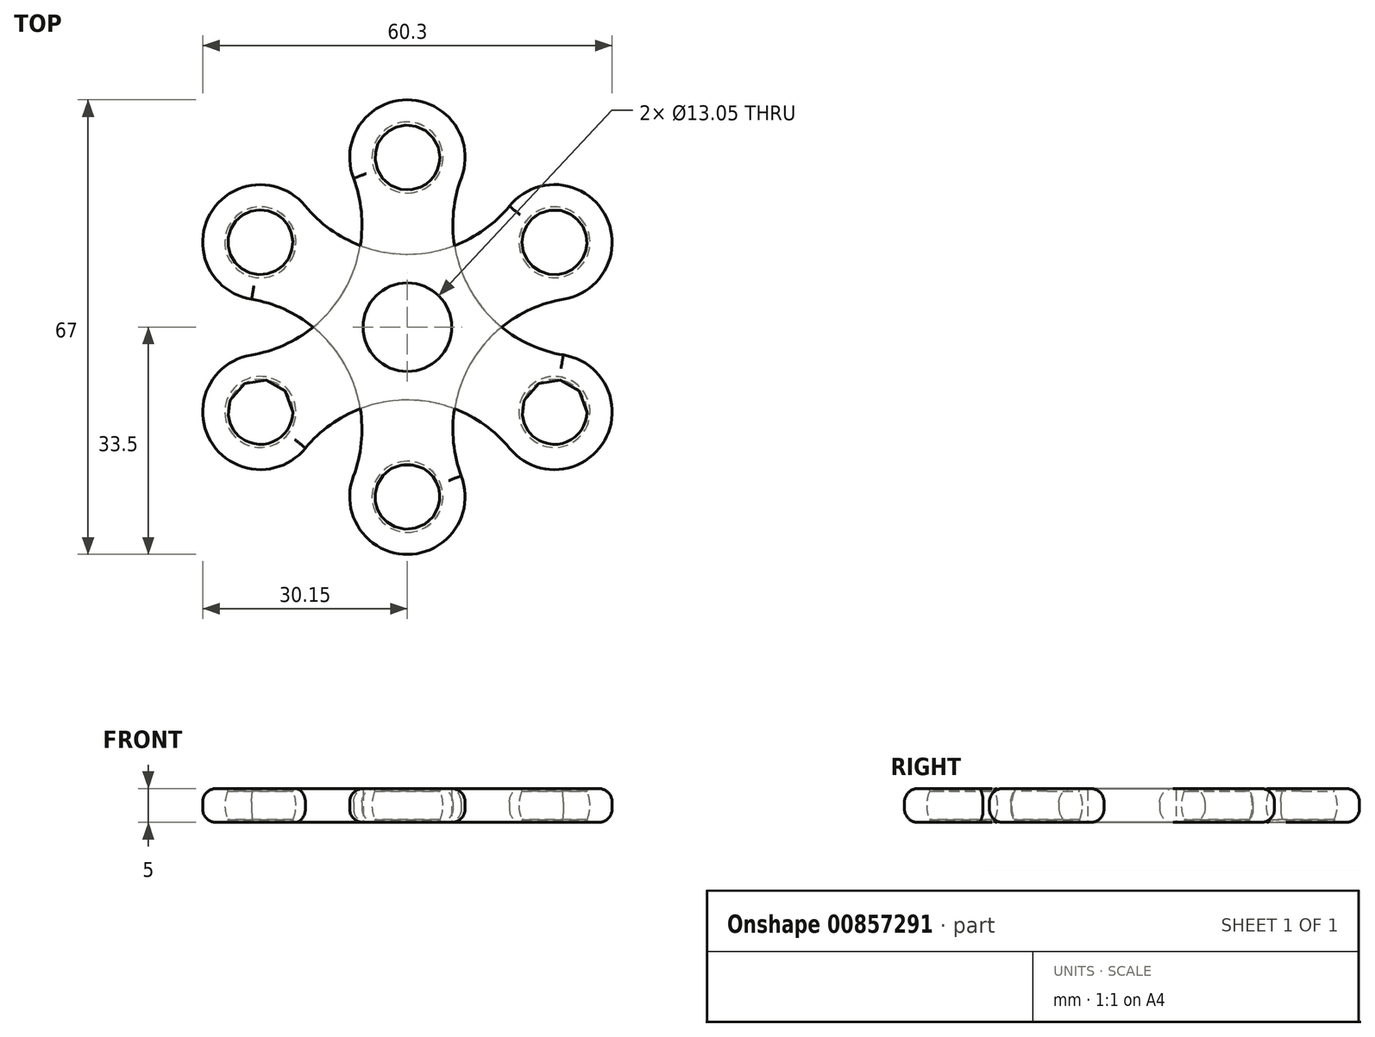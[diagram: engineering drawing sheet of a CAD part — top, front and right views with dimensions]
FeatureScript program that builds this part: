
annotation { "Feature Type Name" : "Feature", "Feature Type Description" : "" }
export const myFeature = defineFeature(function(context is Context, id is Id, definition is map)
    precondition{}
    {
        {
            var Q0;
            Q0=qCreatedBy(makeId("Top.planeOp"),FACE);
            var sketch = newSketch(context, id + "F0", { "sketchPlane" : qUnion([Q0])});
            skCircle(sketch, "E0", {"center": v(0, 0) * mm, "radius": 6.53 * mm});
            skCircle(sketch, "E1", {"center": v(0, 25) * mm, "radius": 2.5 * mm});
            skArc(sketch, "E2", {"start": v(7.95, 22) * mm, "mid": v(-0.05, 33.5) * mm, "end": v(-7.92, 21.91) * mm});
            skArc(sketch, "E3.1.0", {"start": v(-23.03, -4.11) * mm, "mid": v(-29, -16.79) * mm, "end": v(-15.02, -17.82) * mm});
            skCircle(sketch, "E3.1.1", {"center": v(-21.65, -12.5) * mm, "radius": 2.5 * mm});
            skArc(sketch, "E3.2.0", {"start": v(15.05, -17.86) * mm, "mid": v(29.02, -16.73) * mm, "end": v(22.95, -4.1) * mm});
            skCircle(sketch, "E3.2.1", {"center": v(21.65, -12.5) * mm, "radius": 2.5 * mm});
            skArc(sketch, "E4", {"start": v(-23.03, -4.11) * mm, "mid": v(-9.28, 5.41) * mm, "end": v(-7.98, 22.08) * mm});
            skArc(sketch, "E5.1.0", {"start": v(15.07, -17.89) * mm, "mid": v(-0.05, -10.75) * mm, "end": v(-15.13, -17.95) * mm});
            skArc(sketch, "E5.2.0", {"start": v(7.95, 22) * mm, "mid": v(9.33, 5.33) * mm, "end": v(23.12, -4.13) * mm});
            skLineSegment(sketch, "E6", {"start": v(0, 0) * mm, "end": v(0, 25) * mm});
            skLineSegment(sketch, "E7", {"start": v(0, 0) * mm, "end": v(-21.65, -12.5) * mm});
            skLineSegment(sketch, "E8", {"start": v(0, 0) * mm, "end": v(21.65, -12.5) * mm});
            skSolve(sketch);
        }
        {
            var Q0;
            Q0=qSketchRegion(id+"F0",true);
            extrude(context, id + "F1", {"entities" : qUnion([Q0]), "depth" : 2.5 * mm, "offsetDistance" : 25 * mm});
        }
        {
            var Q0;
            Q0=qSketchRegion(id+"F0",true);
            extrude(context, id + "F2", {"entities" : qUnion([Q0]), "operationType" : NewBodyOperationType.ADD, "oppositeDirection" : true, "depth" : 2.5 * mm, "offsetDistance" : 25 * mm});
        }
        {
            var Q0;
            Q0=qCreatedBy(makeId("Top.planeOp"),FACE);
            var sketch = newSketch(context, id + "F3", { "sketchPlane" : qUnion([Q0])});
            skLineSegment(sketch, "E9", {"start": v(0, 0) * mm, "end": v(0, 25) * mm});
            skCircle(sketch, "E10", {"center": v(0, 25) * mm, "radius": 5.23 * mm});
            skLineSegment(sketch, "E11", {"start": v(0, 30.23) * mm, "end": v(0, 25) * mm});
            skSolve(sketch);
        }
        {
            var Q0;
            {var subQ0=sQuery(id+"F3.wireOp",EDGE,"E11");Q0=makeQuery(id+"F3.imprint","IMPRINT",FACE,{"disambiguationData":[TD([[makeQuery(id+"F3.imprint","IMPRINT",EDGE,{"derivedFrom":subQ0}),1.0]])]});}
            var Q1;
            Q1=sQuery(id+"F3.wireOp",EDGE,"E11");
            revolve(context, id + "F4", {"surfaceOperationType" : NewSurfaceOperationType.NEW, "entities" : qUnion([Q0]), "axis" : qUnion([Q1]), "revolveType" : RevolveType.FULL});
        }
        {
            var Q0;
            Q0=qCreatedBy(makeId("Top.planeOp"),FACE);
            var sketch = newSketch(context, id + "F5", { "sketchPlane" : qUnion([Q0])});
            skLineSegment(sketch, "E12", {"start": v(0, 0) * mm, "end": v(0, 25) * mm});
            skLineSegment(sketch, "E13.1.0", {"start": v(0, 0) * mm, "end": v(-21.65, -12.5) * mm});
            skLineSegment(sketch, "E13.2.0", {"start": v(0, 0) * mm, "end": v(21.65, -12.5) * mm});
            skPoint(sketch, "E13.center", {"position": v(0, 0) * mm});
            skCircle(sketch, "E14", {"center": v(-21.65, -12.5) * mm, "radius": 5.23 * mm});
            skLineSegment(sketch, "E15", {"start": v(-21.65, -12.5) * mm, "end": v(-26.18, -15.11) * mm});
            skSolve(sketch);
        }
        {
            var Q0;
            {var subQ0=sQuery(id+"F5.wireOp",EDGE,"E15");Q0=makeQuery(id+"F5.imprint","IMPRINT",FACE,{"disambiguationData":[TD([[makeQuery(id+"F5.imprint","IMPRINT",EDGE,{"derivedFrom":subQ0}),-1.0]])]});}
            var Q1;
            Q1=sQuery(id+"F5.wireOp",EDGE,"E15");
            revolve(context, id + "F6", {"surfaceOperationType" : NewSurfaceOperationType.NEW, "entities" : qUnion([Q0]), "axis" : qUnion([Q1]), "revolveType" : RevolveType.FULL});
        }
        {
            var Q0;
            Q0=qCreatedBy(makeId("Top.planeOp"),FACE);
            var sketch = newSketch(context, id + "F7", { "sketchPlane" : qUnion([Q0])});
            skLineSegment(sketch, "E16", {"start": v(0, 0) * mm, "end": v(0, 25) * mm});
            skLineSegment(sketch, "E17.1.0", {"start": v(0, 0) * mm, "end": v(-21.65, -12.5) * mm});
            skLineSegment(sketch, "E17.2.0", {"start": v(0, 0) * mm, "end": v(21.65, -12.5) * mm});
            skPoint(sketch, "E17.center", {"position": v(0, 0) * mm});
            skCircle(sketch, "E18", {"center": v(21.65, -12.5) * mm, "radius": 5.23 * mm});
            skLineSegment(sketch, "E19", {"start": v(21.65, -12.5) * mm, "end": v(26.18, -15.12) * mm});
            skSolve(sketch);
        }
        {
            var Q0;
            {var subQ0=sQuery(id+"F7.wireOp",EDGE,"E19");Q0=makeQuery(id+"F7.imprint","IMPRINT",FACE,{"disambiguationData":[TD([[makeQuery(id+"F7.imprint","IMPRINT",EDGE,{"derivedFrom":subQ0}),-1.0]])]});}
            var Q1;
            Q1=sQuery(id+"F7.wireOp",EDGE,"E19");
            revolve(context, id + "F8", {"surfaceOperationType" : NewSurfaceOperationType.NEW, "entities" : qUnion([Q0]), "axis" : qUnion([Q1]), "revolveType" : RevolveType.FULL});
        }
        {
            var Q0;
            Q0=makeQuery(id+"F4.opRevolve","SWEPT_BODY",BODY,{"disambiguationData":[OSD([sQuery(id+"F3.wireOp",EDGE,"E9"),sQuery(id+"F3.wireOp",EDGE,"E10"),sQuery(id+"F3.wireOp",EDGE,"E11")])]});
            var Q1;
            Q1=makeQuery(id+"F8.opRevolve","SWEPT_BODY",BODY,{"disambiguationData":[OSD([sQuery(id+"F7.wireOp",EDGE,"E17.2.0"),sQuery(id+"F7.wireOp",EDGE,"E18"),sQuery(id+"F7.wireOp",EDGE,"E19")])]});
            var Q2;
            Q2=makeQuery(id+"F6.opRevolve","SWEPT_BODY",BODY,{"disambiguationData":[OSD([sQuery(id+"F5.wireOp",EDGE,"E13.1.0"),sQuery(id+"F5.wireOp",EDGE,"E14"),sQuery(id+"F5.wireOp",EDGE,"E15")])]});
            var Q3;
            Q3=makeQuery(id+"F1.opExtrude","SWEPT_BODY",BODY,{"disambiguationData":[OSD([sQuery(id+"F0.wireOp",EDGE,"E0"),sQuery(id+"F0.wireOp",EDGE,"E1"),sQuery(id+"F0.wireOp",EDGE,"E2"),sQuery(id+"F0.wireOp",EDGE,"E3.1.0"),sQuery(id+"F0.wireOp",EDGE,"E3.1.1"),sQuery(id+"F0.wireOp",EDGE,"E3.2.0"),sQuery(id+"F0.wireOp",EDGE,"E3.2.1"),sQuery(id+"F0.wireOp",EDGE,"E4"),sQuery(id+"F0.wireOp",EDGE,"E5.1.0"),sQuery(id+"F0.wireOp",EDGE,"E5.2.0")])]});
            booleanBodies(context, id + "F9", {"operationType" : BooleanOperationType.SUBTRACTION, "tools" : qUnion([Q0, Q1, Q2]), "targets" : qUnion([Q3])});
        }
        {
            var Q0;
            Q0=makeQuery(id+"F1.opExtrude","CAP_EDGE",EDGE,{"disambiguationData":[OSD([sQuery(id+"F0.wireOp",EDGE,"E4")])],"isStart":false});
            var Q1;
            Q1=makeQuery(id+"F1.opExtrude","CAP_EDGE",EDGE,{"disambiguationData":[OSD([sQuery(id+"F0.wireOp",EDGE,"E2")])],"isStart":false});
            var Q2;
            {var subQ0=sQuery(id+"F0.wireOp",EDGE,"E5.2.0");Q2=makeQuery(id+"F1.opExtrude","CAP_EDGE",EDGE,{"disambiguationData":[OSD([subQ0]),TDD([makeQuery(id+"F0.imprint","IMPRINT",EDGE,{"disambiguationData":[TD([[makeQuery(id+"F0.imprint","INTERSECT",VERTEX,{"derivedFrom":[sQuery(id+"F0.wireOp",EDGE,"E2"),subQ0]}),-1.0]])],"derivedFrom":subQ0})])],"isStart":false});}
            var Q3;
            {var subQ0=sQuery(id+"F0.wireOp",EDGE,"E3.1.0");Q3=makeQuery(id+"F1.opExtrude","CAP_EDGE",EDGE,{"disambiguationData":[OSD([subQ0]),TDD([makeQuery(id+"F0.imprint","IMPRINT",EDGE,{"disambiguationData":[TD([[makeQuery(id+"F0.imprint","INTERSECT",VERTEX,{"derivedFrom":[subQ0,sQuery(id+"F0.wireOp",EDGE,"E4")]}),-1.0]])],"derivedFrom":subQ0})])],"isStart":false});}
            var Q4;
            {var subQ0=sQuery(id+"F0.wireOp",EDGE,"E5.1.0");Q4=makeQuery(id+"F1.opExtrude","CAP_EDGE",EDGE,{"disambiguationData":[OSD([subQ0]),TDD([makeQuery(id+"F0.imprint","IMPRINT",EDGE,{"disambiguationData":[TD([[makeQuery(id+"F0.imprint","INTERSECT",VERTEX,{"disambiguationData":[OD(0.0)],"derivedFrom":[sQuery(id+"F0.wireOp",EDGE,"E3.1.0"),subQ0]}),1.0]])],"derivedFrom":subQ0})])],"isStart":false});}
            var Q5;
            {var subQ0=sQuery(id+"F0.wireOp",EDGE,"E3.2.0");Q5=makeQuery(id+"F1.opExtrude","CAP_EDGE",EDGE,{"disambiguationData":[OSD([subQ0]),TDD([makeQuery(id+"F0.imprint","IMPRINT",EDGE,{"disambiguationData":[TD([[makeQuery(id+"F0.imprint","INTERSECT",VERTEX,{"derivedFrom":[subQ0,sQuery(id+"F0.wireOp",EDGE,"E5.1.0")]}),-1.0]])],"derivedFrom":subQ0})])],"isStart":false});}
            var Q6;
            {var subQ0=sQuery(id+"F0.wireOp",EDGE,"E5.2.0");var subQ1=sQuery(id+"F0.wireOp",EDGE,"E3.2.0");Q6=makeQuery(id+"F1.opExtrude","CAP_EDGE",EDGE,{"disambiguationData":[OSD([subQ1]),TDD([makeQuery(id+"F0.imprint","IMPRINT",EDGE,{"disambiguationData":[TD([[makeQuery(id+"F0.imprint","INTERSECT",VERTEX,{"disambiguationData":[OD(0.0)],"derivedFrom":[subQ1,subQ0]}),1.0]])],"derivedFrom":subQ1})])],"isStart":false});}
            var Q7;
            {var subQ0=sQuery(id+"F0.wireOp",EDGE,"E5.2.0");var subQ1=sQuery(id+"F0.wireOp",EDGE,"E3.2.0");Q7=makeQuery(id+"F1.opExtrude","CAP_EDGE",EDGE,{"disambiguationData":[OSD([subQ0]),TDD([makeQuery(id+"F0.imprint","IMPRINT",EDGE,{"disambiguationData":[TD([[makeQuery(id+"F0.imprint","INTERSECT",VERTEX,{"disambiguationData":[OD(1.0)],"derivedFrom":[subQ1,subQ0]}),1.0]])],"derivedFrom":subQ0})])],"isStart":false});}
            var Q8;
            {var subQ0=sQuery(id+"F0.wireOp",EDGE,"E5.1.0");var subQ1=sQuery(id+"F0.wireOp",EDGE,"E3.1.0");Q8=makeQuery(id+"F1.opExtrude","CAP_EDGE",EDGE,{"disambiguationData":[OSD([subQ1]),TDD([makeQuery(id+"F0.imprint","IMPRINT",EDGE,{"disambiguationData":[TD([[makeQuery(id+"F0.imprint","INTERSECT",VERTEX,{"disambiguationData":[OD(0.0)],"derivedFrom":[subQ1,subQ0]}),1.0]])],"derivedFrom":subQ1})])],"isStart":false});}
            var Q9;
            {var subQ0=sQuery(id+"F0.wireOp",EDGE,"E5.1.0");var subQ1=sQuery(id+"F0.wireOp",EDGE,"E3.1.0");Q9=makeQuery(id+"F1.opExtrude","CAP_EDGE",EDGE,{"disambiguationData":[OSD([subQ0]),TDD([makeQuery(id+"F0.imprint","IMPRINT",EDGE,{"disambiguationData":[TD([[makeQuery(id+"F0.imprint","INTERSECT",VERTEX,{"disambiguationData":[OD(1.0)],"derivedFrom":[subQ1,subQ0]}),1.0]])],"derivedFrom":subQ0})])],"isStart":false});}
            var Q10;
            {var subQ0=sQuery(id+"F0.wireOp",EDGE,"E5.1.0");Q10=makeQuery(id+"F2.opExtrude","CAP_EDGE",EDGE,{"disambiguationData":[OSD([subQ0]),TDD([makeQuery(id+"F0.imprint","IMPRINT",EDGE,{"disambiguationData":[TD([[makeQuery(id+"F0.imprint","INTERSECT",VERTEX,{"disambiguationData":[OD(0.0)],"derivedFrom":[sQuery(id+"F0.wireOp",EDGE,"E3.1.0"),subQ0]}),1.0]])],"derivedFrom":subQ0})])],"isStart":false});}
            var Q11;
            {var subQ0=sQuery(id+"F0.wireOp",EDGE,"E3.1.0");Q11=makeQuery(id+"F2.opExtrude","CAP_EDGE",EDGE,{"disambiguationData":[OSD([subQ0]),TDD([makeQuery(id+"F0.imprint","IMPRINT",EDGE,{"disambiguationData":[TD([[makeQuery(id+"F0.imprint","INTERSECT",VERTEX,{"derivedFrom":[subQ0,sQuery(id+"F0.wireOp",EDGE,"E4")]}),-1.0]])],"derivedFrom":subQ0})])],"isStart":false});}
            var Q12;
            Q12=makeQuery(id+"F2.opExtrude","CAP_EDGE",EDGE,{"disambiguationData":[OSD([sQuery(id+"F0.wireOp",EDGE,"E4")])],"isStart":false});
            var Q13;
            {var subQ0=sQuery(id+"F0.wireOp",EDGE,"E5.1.0");var subQ1=sQuery(id+"F0.wireOp",EDGE,"E3.1.0");Q13=makeQuery(id+"F2.opExtrude","CAP_EDGE",EDGE,{"disambiguationData":[OSD([subQ0]),TDD([makeQuery(id+"F0.imprint","IMPRINT",EDGE,{"disambiguationData":[TD([[makeQuery(id+"F0.imprint","INTERSECT",VERTEX,{"disambiguationData":[OD(1.0)],"derivedFrom":[subQ1,subQ0]}),1.0]])],"derivedFrom":subQ0})])],"isStart":false});}
            var Q14;
            {var subQ0=sQuery(id+"F0.wireOp",EDGE,"E5.1.0");var subQ1=sQuery(id+"F0.wireOp",EDGE,"E3.1.0");Q14=makeQuery(id+"F2.opExtrude","CAP_EDGE",EDGE,{"disambiguationData":[OSD([subQ1]),TDD([makeQuery(id+"F0.imprint","IMPRINT",EDGE,{"disambiguationData":[TD([[makeQuery(id+"F0.imprint","INTERSECT",VERTEX,{"disambiguationData":[OD(0.0)],"derivedFrom":[subQ1,subQ0]}),1.0]])],"derivedFrom":subQ1})])],"isStart":false});}
            var Q15;
            {var subQ0=sQuery(id+"F0.wireOp",EDGE,"E3.2.0");Q15=makeQuery(id+"F2.opExtrude","CAP_EDGE",EDGE,{"disambiguationData":[OSD([subQ0]),TDD([makeQuery(id+"F0.imprint","IMPRINT",EDGE,{"disambiguationData":[TD([[makeQuery(id+"F0.imprint","INTERSECT",VERTEX,{"derivedFrom":[subQ0,sQuery(id+"F0.wireOp",EDGE,"E5.1.0")]}),-1.0]])],"derivedFrom":subQ0})])],"isStart":false});}
            var Q16;
            Q16=makeQuery(id+"F2.opExtrude","CAP_EDGE",EDGE,{"disambiguationData":[OSD([sQuery(id+"F0.wireOp",EDGE,"E2")])],"isStart":false});
            var Q17;
            {var subQ0=sQuery(id+"F0.wireOp",EDGE,"E5.2.0");Q17=makeQuery(id+"F2.opExtrude","CAP_EDGE",EDGE,{"disambiguationData":[OSD([subQ0]),TDD([makeQuery(id+"F0.imprint","IMPRINT",EDGE,{"disambiguationData":[TD([[makeQuery(id+"F0.imprint","INTERSECT",VERTEX,{"derivedFrom":[sQuery(id+"F0.wireOp",EDGE,"E2"),subQ0]}),-1.0]])],"derivedFrom":subQ0})])],"isStart":false});}
            var Q18;
            {var subQ0=sQuery(id+"F0.wireOp",EDGE,"E5.2.0");var subQ1=sQuery(id+"F0.wireOp",EDGE,"E3.2.0");Q18=makeQuery(id+"F2.opExtrude","CAP_EDGE",EDGE,{"disambiguationData":[OSD([subQ1]),TDD([makeQuery(id+"F0.imprint","IMPRINT",EDGE,{"disambiguationData":[TD([[makeQuery(id+"F0.imprint","INTERSECT",VERTEX,{"disambiguationData":[OD(0.0)],"derivedFrom":[subQ1,subQ0]}),1.0]])],"derivedFrom":subQ1})])],"isStart":false});}
            var Q19;
            {var subQ0=sQuery(id+"F0.wireOp",EDGE,"E5.2.0");var subQ1=sQuery(id+"F0.wireOp",EDGE,"E3.2.0");Q19=makeQuery(id+"F2.opExtrude","CAP_EDGE",EDGE,{"disambiguationData":[OSD([subQ0]),TDD([makeQuery(id+"F0.imprint","IMPRINT",EDGE,{"disambiguationData":[TD([[makeQuery(id+"F0.imprint","INTERSECT",VERTEX,{"disambiguationData":[OD(1.0)],"derivedFrom":[subQ1,subQ0]}),1.0]])],"derivedFrom":subQ0})])],"isStart":false});}
            fillet(context, id + "F10", {"entities" : qUnion([Q0, Q1, Q2, Q3, Q4, Q5, Q6, Q7, Q8, Q9, Q10, Q11, Q12, Q13, Q14, Q15, Q16, Q17, Q18, Q19]), "radius" : 2 * mm, "tangentPropagation" : true, "allowEdgeOverflow" : false});
        }
        {
            var Q0;
            Q0=makeQuery(id+"F9.opBoolean","COPY",FACE,{"derivedFrom":makeQuery(id+"F6.opRevolve","SWEPT_FACE",FACE,{"disambiguationData":[OSD([sQuery(id+"F5.wireOp",EDGE,"E14")])]})});
            var Q1;
            Q1=makeQuery(id+"F9.opBoolean","COPY",FACE,{"derivedFrom":makeQuery(id+"F8.opRevolve","SWEPT_FACE",FACE,{"disambiguationData":[OSD([sQuery(id+"F7.wireOp",EDGE,"E18")])]})});
            var Q2;
            {var subQ0=sQuery(id+"F0.wireOp",EDGE,"E0");Q2=makeQuery(id+"F2.boolean.opBoolean","MERGE",FACE,{"derivedFrom":[makeQuery(id+"F1.opExtrude","SWEPT_FACE",FACE,{"disambiguationData":[OSD([subQ0])]}),makeQuery(id+"F2.opExtrude","SWEPT_FACE",FACE,{"disambiguationData":[OSD([subQ0])]})]});}
            var Q3;
            Q3=makeQuery(id+"F9.opBoolean","COPY",FACE,{"derivedFrom":makeQuery(id+"F4.opRevolve","SWEPT_FACE",FACE,{"disambiguationData":[OSD([sQuery(id+"F3.wireOp",EDGE,"E10")])]})});
            fillet(context, id + "F11", {"entities" : qUnion([Q0, Q1, Q2, Q3]), "radius" : .3 * mm, "tangentPropagation" : true, "allowEdgeOverflow" : false});
        }
        {
            var Q0;
            Q0=makeQuery(id+"F1.opExtrude","SWEPT_BODY",BODY,{"disambiguationData":[OSD([sQuery(id+"F0.wireOp",EDGE,"E0"),sQuery(id+"F0.wireOp",EDGE,"E1"),sQuery(id+"F0.wireOp",EDGE,"E2"),sQuery(id+"F0.wireOp",EDGE,"E3.1.0"),sQuery(id+"F0.wireOp",EDGE,"E3.1.1"),sQuery(id+"F0.wireOp",EDGE,"E3.2.0"),sQuery(id+"F0.wireOp",EDGE,"E3.2.1"),sQuery(id+"F0.wireOp",EDGE,"E4"),sQuery(id+"F0.wireOp",EDGE,"E5.1.0"),sQuery(id+"F0.wireOp",EDGE,"E5.2.0")])]});
            var Q1;
            {var subQ0=sQuery(id+"F0.wireOp",EDGE,"E0");Q1=makeQuery(id+"F11.opFillet","BLEND_EDGE",EDGE,{"blendedFrom":[makeQuery(id+"F2.opExtrude","CAP_EDGE",EDGE,{"disambiguationData":[OSD([subQ0])],"isStart":false}),makeQuery(id+"F2.boolean.opBoolean","MERGE",FACE,{"derivedFrom":[makeQuery(id+"F1.opExtrude","SWEPT_FACE",FACE,{"disambiguationData":[OSD([subQ0])]}),makeQuery(id+"F2.opExtrude","SWEPT_FACE",FACE,{"disambiguationData":[OSD([subQ0])]})]})],"blendedInto":[makeQuery(id+"F2.boolean.opBoolean","MERGE",FACE,{"derivedFrom":[makeQuery(id+"F1.opExtrude","SWEPT_FACE",FACE,{"disambiguationData":[OSD([subQ0])]}),makeQuery(id+"F2.opExtrude","SWEPT_FACE",FACE,{"disambiguationData":[OSD([subQ0])]})]})]});}
            circularPattern(context, id + "F12", {"entities" : qUnion([Q0]), "axis" : qUnion([Q1]), "angle" : 60 * degree, "instanceCount" : 2, "equalSpace" : true});
        }
    });
